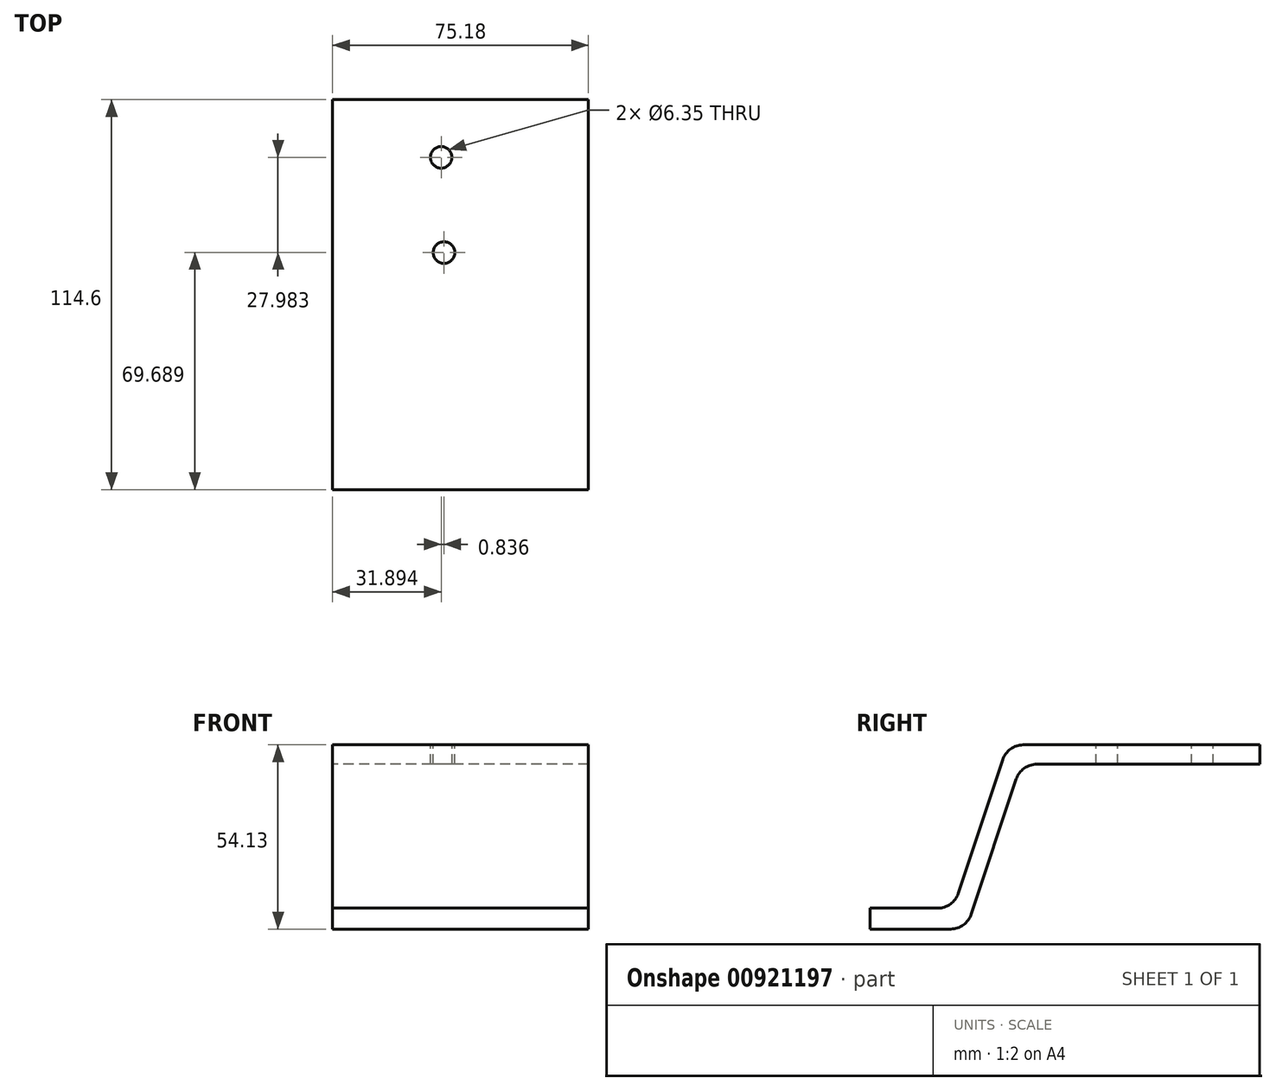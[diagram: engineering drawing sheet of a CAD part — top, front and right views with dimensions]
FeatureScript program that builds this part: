
annotation { "Feature Type Name" : "Feature", "Feature Type Description" : "" }
export const myFeature = defineFeature(function(context is Context, id is Id, definition is map)
    precondition{}
    {
        {
            var Q0;
            Q0=qCreatedBy(makeId("Right.planeOp"),FACE);
            var sketch = newSketch(context, id + "F0", { "sketchPlane" : qUnion([Q0])});
            skLineSegment(sketch, "E0", {"start": v(-55.35, 0) * mm, "end": v(-31.6, 0) * mm});
            skLineSegment(sketch, "E1", {"start": v(-25.57, 4.35) * mm, "end": v(-12.35, 44.1) * mm});
            skLineSegment(sketch, "E2", {"start": v(-6.32, 48.44) * mm, "end": v(59.25, 48.44) * mm});
            skLineSegment(sketch, "E3", {"start": v(59.25, 48.44) * mm, "end": v(59.25, 54.13) * mm});
            skLineSegment(sketch, "E4", {"start": v(59.25, 54.13) * mm, "end": v(-10.3, 54.13) * mm});
            skLineSegment(sketch, "E5", {"start": v(-16.33, 49.78) * mm, "end": v(-29.4, 10.5) * mm});
            skLineSegment(sketch, "E6", {"start": v(-35.42, 6.15) * mm, "end": v(-55.35, 6.15) * mm});
            skLineSegment(sketch, "E7", {"start": v(-55.35, 0) * mm, "end": v(-55.35, 6.15) * mm});
            skPoint(sketch, "E8.visualSharp", {"position": v(-10.9, 48.44) * mm});
            skArc(sketch, "E8.filletArc", {"start": v(-6.32, 48.44) * mm, "mid": v(-10.04, 47.24) * mm, "end": v(-12.35, 44.1) * mm});
            skPoint(sketch, "E9.visualSharp", {"position": v(-14.88, 54.13) * mm});
            skArc(sketch, "E9.filletArc", {"start": v(-10.3, 54.13) * mm, "mid": v(-14.02, 52.93) * mm, "end": v(-16.33, 49.78) * mm});
            skPoint(sketch, "E10.visualSharp", {"position": v(-27.02, 0) * mm});
            skArc(sketch, "E10.filletArc", {"start": v(-31.6, 0) * mm, "mid": v(-27.88, 1.2) * mm, "end": v(-25.57, 4.35) * mm});
            skPoint(sketch, "E11.visualSharp", {"position": v(-30.84, 6.15) * mm});
            skArc(sketch, "E11.filletArc", {"start": v(-35.42, 6.15) * mm, "mid": v(-31.7, 7.35) * mm, "end": v(-29.4, 10.5) * mm});
            skSolve(sketch);
        }
        {
            var Q0;
            Q0=makeQuery(id+"F0.imprint","IMPRINT",FACE,{"disambiguationData":[TD([[makeQuery(id+"F0.imprint","IMPRINT",EDGE,{"derivedFrom":sQuery(id+"F0.wireOp",EDGE,"E0")}),1.0]])]});
            extrude(context, id + "F1", {"entities" : qUnion([Q0]), "depth" : 75.18 * mm, "offsetDistance" : 25.4 * mm});
        }
        {
            var Q0;
            Q0=makeQuery(id+"F1.opExtrude","SWEPT_FACE",FACE,{"disambiguationData":[OSD([sQuery(id+"F0.wireOp",EDGE,"E4")])]});
            var sketch = newSketch(context, id + "F2", { "sketchPlane" : qUnion([Q0])});
            skCircle(sketch, "E12", {"center": v(31.9, 42.32) * mm, "radius": 5.3 * mm});
            skCircle(sketch, "E13", {"center": v(32.73, 14.34) * mm, "radius": 8.12 * mm});
            skCircle(sketch, "E14", {"center": v(79.77, -91.81) * mm, "radius": 5.68 * mm});
            skSolve(sketch);
        }
        {
            var Q0;
            Q0=sQuery(id+"F2.wireOp",VERTEX,"E12.center");
            var Q1;
            Q1=sQuery(id+"F2.wireOp",VERTEX,"E13.center");
            var Q2;
            Q2=sQuery(id+"F2.wireOp",VERTEX,"E14.center");
            var Q3;
            Q3=makeQuery(id+"F1.opExtrude","SWEPT_BODY",BODY,{"disambiguationData":[OSD([sQuery(id+"F0.wireOp",EDGE,"E0"),sQuery(id+"F0.wireOp",EDGE,"E1"),sQuery(id+"F0.wireOp",EDGE,"E2"),sQuery(id+"F0.wireOp",EDGE,"E3"),sQuery(id+"F0.wireOp",EDGE,"E4"),sQuery(id+"F0.wireOp",EDGE,"E5"),sQuery(id+"F0.wireOp",EDGE,"E6"),sQuery(id+"F0.wireOp",EDGE,"E7"),sQuery(id+"F0.wireOp",EDGE,"E8.filletArc"),sQuery(id+"F0.wireOp",EDGE,"E9.filletArc"),sQuery(id+"F0.wireOp",EDGE,"E10.filletArc"),sQuery(id+"F0.wireOp",EDGE,"E11.filletArc")])]});
            hole(context, id + "F3", {"style" : HoleStyle.SIMPLE, "endStyle" : HoleEndStyle.THROUGH, "holeDiameter" : 6.35 * mm, "majorDiameter" : 6.35 * mm, "isTappedThrough" : true, "tappedDepth" : 12.7 * mm, "tapClearance" : 3, "locations" : qUnion([Q0, Q1, Q2]), "scope" : qUnion([Q3])});
        }
    });
